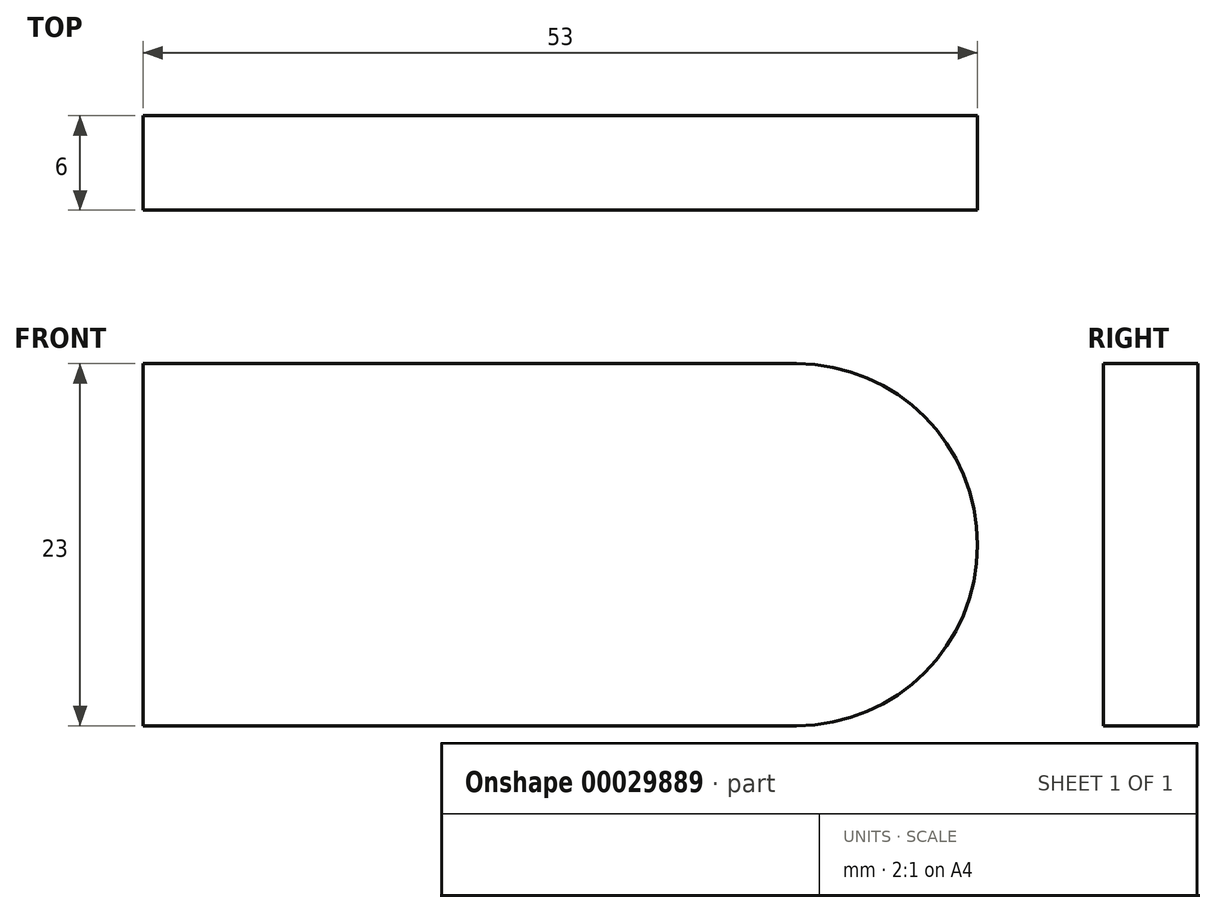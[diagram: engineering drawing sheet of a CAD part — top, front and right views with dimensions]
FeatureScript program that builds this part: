
annotation { "Feature Type Name" : "Feature", "Feature Type Description" : "" }
export const myFeature = defineFeature(function(context is Context, id is Id, definition is map)
    precondition{}
    {
        {
            var Q0;
            Q0=qCreatedBy(makeId("Front.planeOp"),FACE);
            var sketch = newSketch(context, id + "F0", { "sketchPlane" : qUnion([Q0])});
            skLineSegment(sketch, "E0.rect.bottom", {"start": v(-20.75, 11.5) * mm, "end": v(20.75, 11.5) * mm});
            skLineSegment(sketch, "E0.rect.top", {"start": v(-20.75, -11.5) * mm, "end": v(20.75, -11.5) * mm});
            skLineSegment(sketch, "E0.rect.left", {"start": v(-20.75, 11.5) * mm, "end": v(-20.75, -11.5) * mm});
            skLineSegment(sketch, "E0.rect.right", {"start": v(20.75, 11.5) * mm, "end": v(20.75, -11.5) * mm, "construction": true});
            skPoint(sketch, "E0.rect.middle", {"position": v(0, 0) * mm});
            skArc(sketch, "E1", {"start": v(20.75, 11.5) * mm, "mid": v(32.25, 0) * mm, "end": v(20.75, -11.5) * mm});
            skSolve(sketch);
        }
        {
            var Q0;
            Q0 = qSketchRegion(id + "F0", true);
            extrude(context, id + "F1", {"entities" : qUnion([Q0]), "endBound" : BoundingType.SYMMETRIC, "depth" : 6 * mm});
        }
    });
